# Revit family: LAMP_OCULT SYSTEM CORNER
name_source: partatom
category: Luminarias
revit_build: Autodesk Revit 2015 (Build: 20140606_1530(x64)
units: mm (PartAtom-declared; Revit-internal decimal feet)

## types (4) — shared parameters
Comentarios de tipo = Availability of changing profile version and height when placed in project.
Dimensions = 100x100x96
Elevación por defecto = 1219 mm
Fabricante = LAMP
IEE = A+
Installation instructions = https://www.lamp.es
Insulation class = I
Last update = 31/07/2019
Luminaire type = Profile
Manufacturer URL = http://www.lamp.es
Manufacturer country = Spain
Manufacturer name = LAMP
Material suspension = Panel de metal
Model explanation = Availability of changing profile version and height when placed in project.
Product URL = https://www.lamp.es
Product datasheet = http://www.lamp.es
Protection rating = IP20

## per-type parameters (varying)
| type | Descripción | Finish | Material perfil | Recessed dimensions | Weight |
| OSRECR100B | OCULT SYS. ACC. REC CORNER 100 BK. | Matte black RAL 9011 | LAMP_Aluminio Ocult Pendular NG |  | 0.43 kg |
| OSRECR100W | OCULT SYS. ACC. REC CORNER 100 WH. | Matte white RAL 9010 | LAMP_Aluminio Ocult Pendular BL |  | 0.43 kg |
| OSSUCR100B | OCULT SYS. ACC. SUR CORNER 100 BK. | Matte black RAL 9011 | LAMP_Aluminio Ocult Pendular NG | 110x110x59 | 0.42 kg |
| OSSUCR100W | OCULT SYS. ACC. SUR CORNER 100 WH. | Matte white RAL 9010 | LAMP_Aluminio Ocult Pendular BL | 110x110x59 | 0.42 kg |

note: column(s) folded — value = type name in every type: Modelo, Product code
